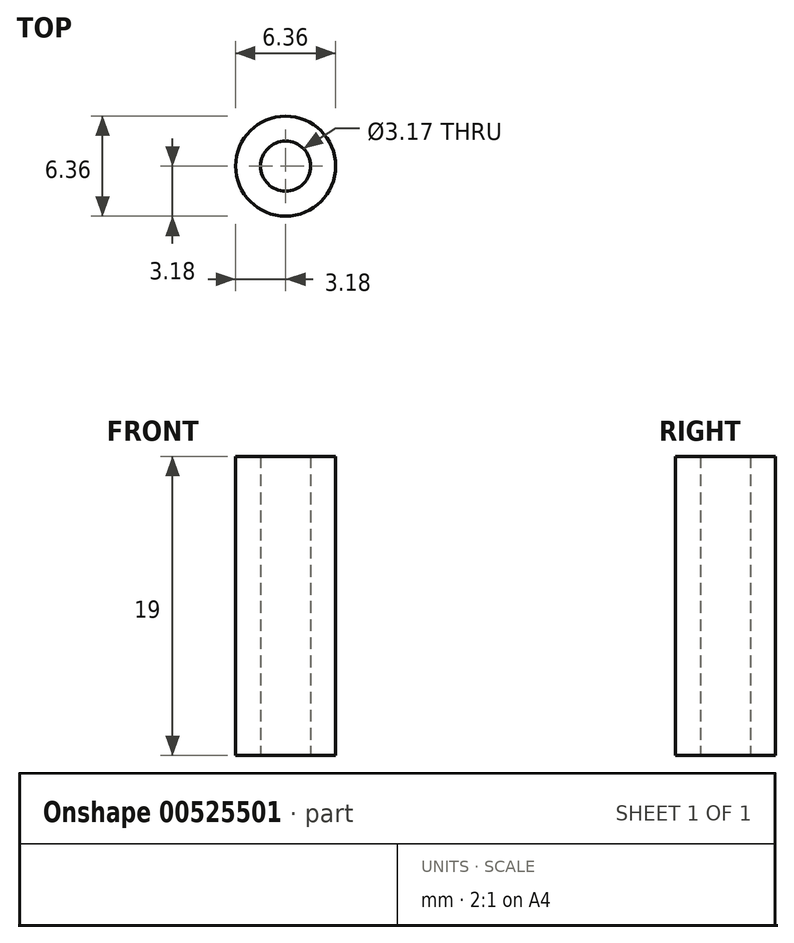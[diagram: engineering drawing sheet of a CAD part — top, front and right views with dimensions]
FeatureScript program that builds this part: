
annotation { "Feature Type Name" : "Feature", "Feature Type Description" : "" }
export const myFeature = defineFeature(function(context is Context, id is Id, definition is map)
    precondition{}
    {
        {
            var Q0;
            Q0=qCreatedBy(makeId("Top.planeOp"),FACE);
            var sketch = newSketch(context, id + "F0", { "sketchPlane" : qUnion([Q0])});
            skCircle(sketch, "E0", {"center": v(0, 0) * mm, "radius": 1.59 * mm});
            skCircle(sketch, "E1", {"center": v(0, 0) * mm, "radius": 3.17 * mm});
            skSolve(sketch);
        }
        {
            var Q0;
            Q0 = qSketchRegion(id + "F0", true);
            extrude(context, id + "F1", {"entities" : qUnion([Q0]), "depth" : 19 * mm, "offsetDistance" : 25 * mm});
        }
    });
